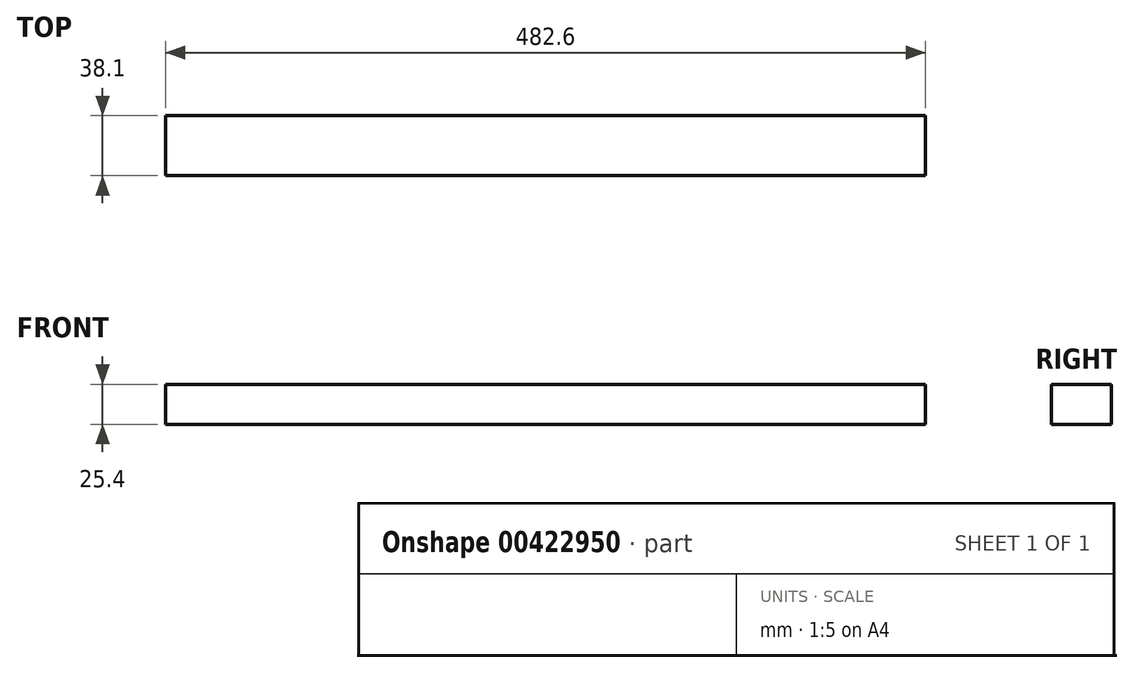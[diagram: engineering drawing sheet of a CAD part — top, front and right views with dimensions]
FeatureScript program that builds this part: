
annotation { "Feature Type Name" : "Feature", "Feature Type Description" : "" }
export const myFeature = defineFeature(function(context is Context, id is Id, definition is map)
    precondition{}
    {
        {
            var Q0;
            Q0=qCreatedBy(makeId("Front.planeOp"),FACE);
            var sketch = newSketch(context, id + "F0", { "sketchPlane" : qUnion([Q0])});
            skLineSegment(sketch, "E0.bottom", {"start": v(241.3, 12.7) * mm, "end": v(-241.3, 12.7) * mm});
            skLineSegment(sketch, "E0.top", {"start": v(241.3, -12.7) * mm, "end": v(-241.3, -12.7) * mm});
            skLineSegment(sketch, "E0.left", {"start": v(241.3, 12.7) * mm, "end": v(241.3, -12.7) * mm});
            skLineSegment(sketch, "E0.right", {"start": v(-241.3, 12.7) * mm, "end": v(-241.3, -12.7) * mm});
            skPoint(sketch, "E0.middle", {"position": v(0, 0) * mm});
            skSolve(sketch);
        }
        {
            var Q0;
            Q0 = qSketchRegion(id + "F0", true);
            extrude(context, id + "F1", {"entities" : qUnion([Q0]), "depth" : 38.1 * mm, "offsetDistance" : 25.4 * mm});
        }
    });
